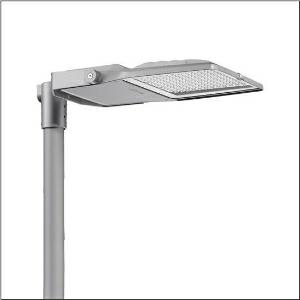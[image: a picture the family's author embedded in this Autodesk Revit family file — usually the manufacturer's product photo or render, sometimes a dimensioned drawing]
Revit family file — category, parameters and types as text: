
# Revit family: floodlight_fl_21_iq_midi___pl52_5xa7782e2d3a_7997
name_source: partatom
category: Lighting Fixtures
units: mm (PartAtom-declared; Revit-internal decimal feet)

## family parameters
Cut with Voids When Loaded = No
Host = Face
Light Source = No
Part Type = Normal
Room Calculation Point = No
Round Connector Dimension = Use Diameter
Shared = No

## types (1)
- --- (1 x LED, 26850 lm, 208.1 W, 3000K)
    Apparent Load = 208 VA
    CIE Flux Codes = 26 60 98 100 100
    Color Rendering = 70
    Color Temperature = 3000K
    Default Elevation = 1800 mm
    Description = Floodlight FL 21 iQ midi, floodlight, primary light control with lens, of PMMA, primary optical cover: protective disc, of toughened safety glass, transparent, light distribution: PL52, light emission: direct distribution, installation type: surface-mounted, LED, High Power LED, rated luminous flux: 26.850lm, luminous efficacy: 129lm/W, light colour: 730, colour temperature: 3000K, control gear: iQ Street-Remote/DALI, control: optimised constant luminous flux control (CLO 2.0), Desk-Remote (wireless, voltage-free reading and setting of iQ features in the workshop via application-optimized NFC function/RFID function), Smart-Wire, Night-Set, Temp-Guard, Auto-Match, Street-Remote, with terminal, 6-pole, mains connection: 220..240V, AC, 50/60Hz, start of lifetime: 208W, end of service life: 227W, reduction: 90W, luminaire housing, of diecast aluminium, powder-coated, Siteco® metallic grey (DB 702S), corrosivity category C5 mid according to DIN EN ISO 12944, suitable for swimming pools, chlorine-resistant, sealing non-destructively replaceable, please order mast flange separately, mast bracket, of steel, galvanised, powder-coated, Siteco® metallic grey (DB 702S), protection rating (complete): IP66, insulation class (complete): insulation class II (safety insulation), certification: CE, ENEC, VDE, protection symbol: D, impact resistance: IK08, permissible operating ambient temperature: -40..+40°C, permissible operating ambient temperature for outdoor applications: -40..+50°C, standard: DIN EN 12944, LABS conformity tested according to VDMA 24364:2018-05, packaging unit: 1 piece

Light Distribution: PL52
    Height = 76 mm
    Lamp = 1 x LED
    Lamp Light Flux = 26850 lm
    Lamp Power = 208.1 W
    Lamp count = 1
    Length = 657 mm
    Luminous efficacy = 129 lm/W
    Manufacturer = Siteco
    ModVariant = No
    Model = 5XA7782E2D3A
    Number of Poles = 1
    OnlyDefault = Yes
    Power Factor = 1
    Product Name = Floodlight FL 21 iQ midi | PL52
    Product group = floodlight | pylon annexe
    ProductGroupID = 6200
    Protection Class = Protection class II
    Protection Degree = IP 66
    RLX_Detail_Level = 1
    RLX_Emergency_Light_Flux = 0 lm
    RLX_Emergency_Type = 0
    RLX_Emergency_Type_DB = No
    RlxData = <blob elided: 153993 chars, md5=87f4e6c2>
    Socket = socket
    Standby Power = 0 W
    System Light Flux = 26850 lm
    System Power = 208 W
    Type Comments = factory setting: luminous flux: 100 % | dim-lin: 254 | 710 mA
    Type Image = l_1007123.jpg
    URL = http://relux.com
    VarID = @adj_106086
    Voltage = 0 V
    Weight = 0.00 kg
    Width = 442 mm

## geometry (parser evidence)
native form markers: Blend x4, Sweep x14
no freeform markers — native parametric forms only
